# Revit family: bimlib_narujnyeblokisistemakondicionirovaniya_mrv_iii-c_plus_haier
name_source: partatom
category: Оборудование
units: mm (PartAtom-declared; Revit-internal decimal feet)

## family parameters
Всегда вертикально = Да
На основе рабочей плоскости = Нет
Общий = Нет
При загрузке вырезать с полостями = Нет
Размер круглого соединителя = Использовать диаметр
Тип детали = Нормальный
Точка расчета площади = Нет

## types (5) — shared parameters
ADSK_URL документации изделия = https://haierproff.ru
ADSK_URL страницы изделия = https://haierproff.ru
ADSK_Версия Revit = 2017
ADSK_Группирование = VRF-системы MRV III-C plus
ADSK_Единица измерения = шт.
ADSK_Завод-изготовитель = Haier Group
ADSK_Классификация нагрузок = ОВК
ADSK_Количество = 1
ADSK_Количество фаз = 3
ADSK_Коэффициент мощности = 1
ADSK_Напряжение = 400 В
ADSK_Обозначение = MRV III-C plus
ADSK_Размер_Высота = 1808 мм
ADSK_Размер_Глубина = 750 мм
BL_BIM library = https://bimlib.pro
HG_URL поставщика = www.haierproff.ru
URL = www.haier.com
Изготовитель = Haier Group
Производитель компрессора = MITSUBISHI ELECTRIC
Работа на обогрев = Нет
Рабочий диапазон_Обогрев = -23 ~ 21
Рабочий диапазон_Охлаждение = -5 ~ 50
Сбоку = Подключение : Сбоку
Снизу = Подключение : Снизу
Спереди = Подключение : Спереди
Тип компрессора = DC INV. СПИРАЛ.
Тип хладагента = R410A
Частота тока = 50 Гц
zero-valued in all types: Отметка по умолчанию

## per-type parameters (varying)
- AV08IMSEVA_8HP_HAIER: 12-16HP=Нет; 8-10HP=Да; ADSK_Код изделия=AV08IMSEVA; ADSK_Масса=220; ADSK_Наименование=Наружный блок VRF-системы кондиционирования MRV III-C plus, 8HP; ADSK_Наименование краткое=VRF-системы MRV III-C plus, 8HP; ADSK_Номинальная мощность=5830 Вт; ADSK_Полная мощность=5830 В·А; ADSK_Размер_Ширина=990 мм; ADSK_Расход воздуха=12200.0 м³/ч; Диаметр_Газ=19.05 мм; Диаметр_Жидкость=9.52 мм; Заправка хладагента=7.00 кг; Звуковая мощность=73; Звуковое давление=57; Обогрев_Максимальная потребляемая мощность=13 кВт; Обогрев_Максимальный ток=21 А; Обогрев_Номинальная потребляемая мощность=6 кВт; Обогрев_Номинальный ток=10 А; Охлаждение_Максимальная потребляемая мощность=14 кВт; Охлаждение_Максимальный ток=23 А; Охлаждение_Номинальная потребляемая мощность=6 кВт; Охлаждение_Номинальный ток=10 А; Теплопроизводительность=27 кВт; Холодопроизводительность=25 кВт
- AV12IMSEVA_12HP_HAIER: 12-16HP=Да; 8-10HP=Нет; ADSK_Код изделия=AV12IMSEVA; ADSK_Масса=276; ADSK_Наименование=Наружный блок VRF-системы кондиционирования MRV III-C plus, 12HP; ADSK_Наименование краткое=VRF-системы MRV III-C plus, 12HP; ADSK_Номинальная мощность=9240 Вт; ADSK_Полная мощность=9240 В·А; ADSK_Размер_Ширина=1390 мм; ADSK_Расход воздуха=14100.0 м³/ч; Диаметр_Газ=25.4 мм; Диаметр_Жидкость=12.7 мм; Заправка хладагента=8.50 кг; Звуковая мощность=76; Звуковое давление=59; Обогрев_Максимальная потребляемая мощность=15 кВт; Обогрев_Максимальный ток=25 А; Обогрев_Номинальная потребляемая мощность=9 кВт; Обогрев_Номинальный ток=15 А; Охлаждение_Максимальная потребляемая мощность=17 кВт; Охлаждение_Максимальный ток=27 А; Охлаждение_Номинальная потребляемая мощность=9 кВт; Охлаждение_Номинальный ток=15 А; Теплопроизводительность=38 кВт; Холодопроизводительность=34 кВт
- AV10IMSEVA_10HP_HAIER: 12-16HP=Нет; 8-10HP=Да; ADSK_Код изделия=AV10IMSEVA; ADSK_Масса=220; ADSK_Наименование=Наружный блок VRF-системы кондиционирования MRV III-C plus, 10HP; ADSK_Наименование краткое=VRF-системы MRV III-C plus, 10HP; ADSK_Номинальная мощность=7180 Вт; ADSK_Полная мощность=7180 В·А; ADSK_Размер_Ширина=990 мм; ADSK_Расход воздуха=12200.0 м³/ч; Диаметр_Газ=22.22 мм; Диаметр_Жидкость=9.52 мм; Заправка хладагента=7.00 кг; Звуковая мощность=73; Звуковое давление=57; Обогрев_Максимальная потребляемая мощность=13 кВт; Обогрев_Максимальный ток=22 А; Обогрев_Номинальная потребляемая мощность=8 кВт; Обогрев_Номинальный ток=12 А; Охлаждение_Максимальная потребляемая мощность=14 кВт; Охлаждение_Максимальный ток=24 А; Охлаждение_Номинальная потребляемая мощность=7 кВт; Охлаждение_Номинальный ток=12 А; Теплопроизводительность=32 кВт; Холодопроизводительность=28 кВт
- AV14IMSEVA_14HP_HAIER: 12-16HP=Да; 8-10HP=Нет; ADSK_Код изделия=AV14IMSEVA; ADSK_Масса=276; ADSK_Наименование=Наружный блок VRF-системы кондиционирования MRV III-C plus, 14HP; ADSK_Наименование краткое=VRF-системы MRV III-C plus, 14HP; ADSK_Номинальная мощность=10800 Вт; ADSK_Полная мощность=10800 В·А; ADSK_Размер_Ширина=1390 мм; ADSK_Расход воздуха=15200.0 м³/ч; Диаметр_Газ=25.4 мм; Диаметр_Жидкость=12.7 мм; Заправка хладагента=8.50 кг; Звуковая мощность=76; Звуковое давление=59; Обогрев_Максимальная потребляемая мощность=16 кВт; Обогрев_Максимальный ток=25 А; Обогрев_Номинальная потребляемая мощность=11 кВт; Обогрев_Номинальный ток=18 А; Охлаждение_Максимальная потребляемая мощность=17 кВт; Охлаждение_Максимальный ток=28 А; Охлаждение_Номинальная потребляемая мощность=11 кВт; Охлаждение_Номинальный ток=17 А; Теплопроизводительность=45 кВт; Холодопроизводительность=40 кВт
- AV16IMSEVA_16HP_HAIER: 12-16HP=Да; 8-10HP=Нет; ADSK_Код изделия=AV16IMSEVA; ADSK_Масса=296; ADSK_Наименование=Наружный блок VRF-системы кондиционирования MRV III-C plus, 16HP; ADSK_Наименование краткое=VRF-системы MRV III-C plus, 16HP; ADSK_Номинальная мощность=12610 Вт; ADSK_Полная мощность=12610 В·А; ADSK_Размер_Ширина=1390 мм; ADSK_Расход воздуха=15200.0 м³/ч; Диаметр_Газ=28.58 мм; Диаметр_Жидкость=12.7 мм; Заправка хладагента=10.00 кг; Звуковая мощность=76; Звуковое давление=60; Обогрев_Максимальная потребляемая мощность=17 кВт; Обогрев_Максимальный ток=27 А; Обогрев_Номинальная потребляемая мощность=13 кВт; Обогрев_Номинальный ток=20 А; Охлаждение_Максимальная потребляемая мощность=20 кВт; Охлаждение_Максимальный ток=32 А; Охлаждение_Номинальная потребляемая мощность=13 кВт; Охлаждение_Номинальный ток=20 А; Теплопроизводительность=50 кВт; Холодопроизводительность=45 кВт
